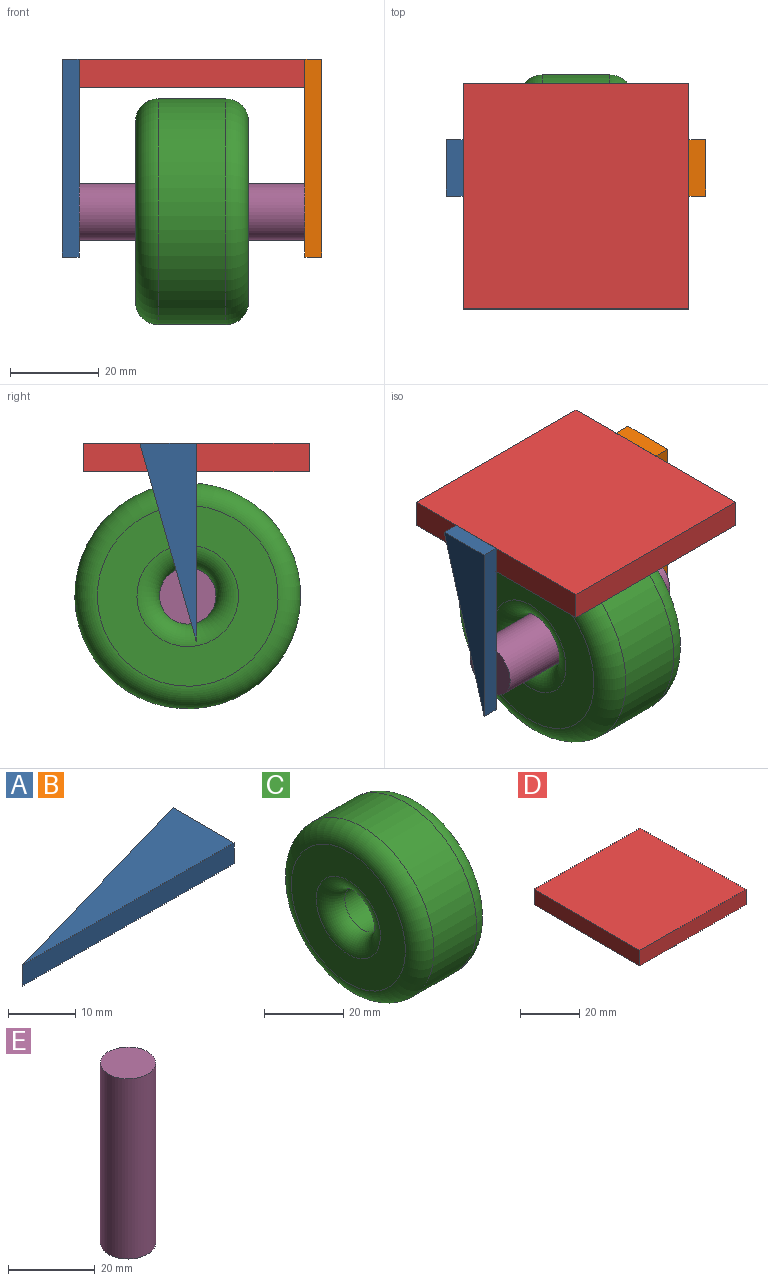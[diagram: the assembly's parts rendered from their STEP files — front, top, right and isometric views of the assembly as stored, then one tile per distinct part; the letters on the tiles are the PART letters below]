
ASSEMBLY  parts=5 mates=4
PART A: 5 faces, bbox 44.5x12.7x3.8 mm
  f0: plane 44.45x12.7mm, normal (-0.27,0.96,0), area 176.1mm2, adj f1,f2,f3,f4
  f1: plane 44.45x3.81mm, normal (0,-1,0), area 169.4mm2, adj f0,f2,f3,f4
  f2: plane 12.7x3.81mm, normal (1,0,0), area 48.4mm2, adj f0,f1,f3,f4
  f3: plane 44.45x12.7mm, normal (0,0,1), area 282.3mm2, adj f0,f1,f2
  f4: plane 44.45x12.7mm, normal (0,0,-1), area 282.3mm2, adj f0,f1,f2
PART B: same geometry as A
PART C: 8 faces, bbox 25.4x55x55 mm
  f0: cylinder r=6.35mm len=15.24mm, axis (-1,0,0), area 608mm2, adj f4,f6
  f1: cylinder r=25.4mm len=50.8mm, axis (-1,0,0), area 2432.2mm2, adj f5,f7
  f2: plane 40.64x40.64mm, normal (1,0,0), area 886.7mm2, adj f4,f5
  f3: plane 40.64x40.64mm, normal (-1,0,0), area 886.7mm2, adj f6,f7
  f4: torus R=11.43mm, axis (1,0,0), area 410.9mm2, adj f0,f2
  f5: torus R=20.32mm, axis (1,0,0), area 1180.9mm2, adj f1,f2
  f6: torus R=11.43mm, axis (1,0,0), area 410.9mm2, adj f0,f3
  f7: torus R=20.32mm, axis (1,0,0), area 1180.9mm2, adj f1,f3
PART D: 6 faces, bbox 50.8x50.8x6.4 mm
  f0: plane 50.8x6.35mm, normal (-1,0,0), area 322.6mm2, adj f1,f3,f4,f5
  f1: plane 50.8x6.35mm, normal (0,-1,0), area 322.6mm2, adj f0,f2,f4,f5
  f2: plane 50.8x6.35mm, normal (1,0,0), area 322.6mm2, adj f1,f3,f4,f5
  f3: plane 50.8x6.35mm, normal (0,1,0), area 322.6mm2, adj f0,f2,f4,f5
  f4: plane 50.8x50.8mm, normal (0,0,1), area 2580.6mm2, adj f0,f1,f2,f3
  f5: plane 50.8x50.8mm, normal (0,0,-1), area 2580.6mm2, adj f0,f1,f2,f3
PART E: 3 faces, bbox 12.7x12.7x50.8 mm
  f0: cylinder r=6.35mm len=50.8mm, axis (0,0,-1), area 2026.8mm2, adj f1,f2
  f1: plane 12.7x12.7mm, normal (0,0,1), area 126.7mm2, adj f0
  f2: plane 12.7x12.7mm, normal (0,0,-1), area 126.7mm2, adj f0
PLACE A rot(axis=(0,-1,0),90deg) t=(-76.56,-49.86,-30.21)mm
PLACE B rot(axis=(0,-1,0),90deg) t=(-21.95,-49.86,-30.21)mm
PLACE C rot(axis=(1,0,0),152.1deg) t=(-63.86,-0.86,-13.77)mm
PLACE D t=(0,-47.12,14.17)mm
PLACE E rot(axis=(-0.58,0.58,-0.58),120deg) t=(-76.56,-51.1,-39.67)mm
MATE revolute E.f0 <-> C.f0  axis (-1,0,0) through (-51.16,-0.86,-13.77)mm
MATE fastened A.f4 <-> D.f0  axis (1,0,0) through (-76.56,-2.76,20.52)mm
MATE fastened E.f0 <-> B.f3  axis (1,0,0) through (-25.76,-0.86,-13.77)mm
MATE fastened B.f3 <-> D.f2  axis (-1,0,0) through (-25.76,-2.76,20.52)mm
